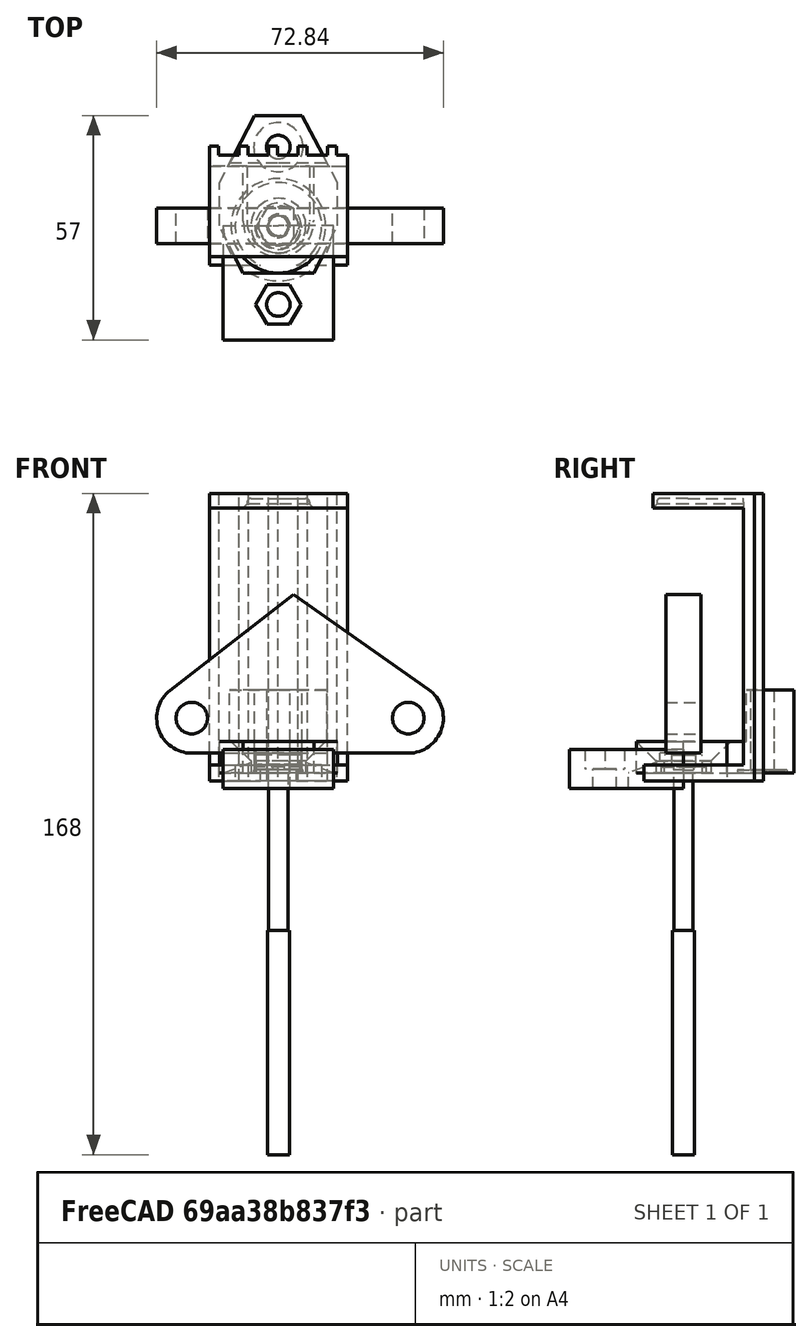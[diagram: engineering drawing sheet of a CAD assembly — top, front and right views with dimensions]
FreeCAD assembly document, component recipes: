
FREECAD ASSEMBLY — COMPONENT RECIPES ("stopper")

This assembly document has 6 components, labeled P0..P5 below (a component is one placed body or linked part). 5 of them carry a construction recipe — the FreeCAD feature program that regenerates the part from scratch, quoted from this document or its linked companion documents; the rest are supplied as boundary geometry only. No exploded tour is included for this assembly.
COMPONENT P0 — recipe-attached ("Body", modeled in this document).
Construction recipe (the document's own serialized feature program — sketch geometry with constraints, then the solid features built on it; lengths are millimeters unless a unit is written):

FEATURE [PartDesign::FeatureBase] BaseFeature
  BaseFeature = -> Extrude
  Suppressed = false
FEATURE [PartDesign::Body] Body004  label="Body"
  AllowCompound = false
  BaseFeature = -> Extrude
  Group = -> [BaseFeature]
  Origin = -> Origin005
  Tip = -> BaseFeature
COMPONENT P1 — geometry summary ("boss001"; no construction recipe available for this part):
  bounding box: 72.8 x 40.3 x 9.0 mm
  tessellated surface: 1,432 triangles
  volume: 16355 mm^3 (62% of its bounding box)
  symmetry: mirror-symmetric across its y mid-plane
COMPONENT P2 — recipe-attached ("fing001", modeled in this document).
Construction recipe (the document's own serialized feature program — sketch geometry with constraints, then the solid features built on it; lengths are millimeters unless a unit is written):

FEATURE [Sketcher::SketchObject] Sketch017  label="cope"
  ArcFitTolerance = 1e-06
  FullyConstrained = true
  MakeInternals = false
  Placement = pos=(0,0,0) rot=(1,0,0;1.5708rad)
  sketch-geometry (6):
    g0: LineSegment StartX=14 StartY=0 StartZ=0 EndX=6 EndY=3 EndZ=0
    g1: LineSegment StartX=6 StartY=3 StartZ=0 EndX=6 EndY=5 EndZ=0
    g2: LineSegment StartX=6 StartY=5 StartZ=0 EndX=0 EndY=5 EndZ=0
    g3: LineSegment StartX=14 StartY=0 StartZ=0 EndX=14 EndY=6 EndZ=0
    g4: LineSegment StartX=14 StartY=6 StartZ=0 EndX=0 EndY=6 EndZ=0
    g5: LineSegment StartX=0 StartY=6 StartZ=0 EndX=0 EndY=5 EndZ=0
  constraints (18):
    c: DistanceY(g0,g0) = 3
    c: Distance(g0,g-2) = 6
    c: Coincident(g0,g1)
    c: Vertical(g1)
    c: Coincident(g1,g2)
    c: PointOnObject(g2,g-2)
    c: Horizontal(g2)
    c: DistanceY(g1,g1) = 2
    c: PointOnObject(g0,g-1)
    c: DistanceX(g-1,g0) = 14
    c: Coincident(g0,g3)
    c: Vertical(g3)
    c: Coincident(g3,g4)
    c: PointOnObject(g4,g-2)
    c: Horizontal(g4)
    c: Coincident(g4,g5)
    c: Coincident(g5,g2)
    c: DistanceY(g3,g3) = 6
FEATURE [PartDesign::Revolution] Revolution
  Angle = 180
  Angle2 = 60
  Axis = (0,-2e-16,1)
  Base = (0,0,0)
  Placement = pos=(0,0,0) rot=(1,0,0;1.5708rad)
  Profile = -> Sketch017
  ReferenceAxis = -> Sketch017 [V_Axis]
  Reversed = true
  Suppressed = false
  Type = 0
FEATURE [Sketcher::SketchObject] Sketch018
  ArcFitTolerance = 1e-06
  AttachmentSupport = -> [Revolution]
  ExternalGeometry = -> [Revolution]
  FullyConstrained = true
  MakeInternals = false
  MapMode = 5
  Placement = pos=(0,0,6) rot=(0,0,1;3.14159rad)
  sketch-geometry (7):
    g0: LineSegment StartX=14 StartY=0 StartZ=0 EndX=14 EndY=29 EndZ=0
    g1: LineSegment StartX=14 StartY=29 StartZ=0 EndX=-14 EndY=29 EndZ=0
    g2: LineSegment StartX=-14 StartY=29 StartZ=0 EndX=-14 EndY=-3.6e-15 EndZ=0
    g3: GeomPoint X=0 Y=20 Z=0
    g4: GeomPoint X=0 Y=29 Z=0
    g5: GeomPoint X=0 Y=14 Z=0
    g6: ArcOfCircle CenterX=4.208e-13 CenterY=2.6e-15 CenterZ=0 NormalX=0 NormalY=0 NormalZ=1 AngleXU=0 Radius=14 StartAngle=0 EndAngle=3.14159
  constraints (15):
    c: Coincident(g0,g1)
    c: Coincident(g1,g2)
    c: Vertical(g0)
    c: Vertical(g2)
    c: Horizontal(g1)
    c: Coincident(g0,g-3)
    c: Coincident(g-4,g2)
    c: PointOnObject(g3,g-2)
    c: Symmetric(g1,g1,g4)
    c: DistanceY(g3,g4) = 9
    c: DistanceY(g-1,g3) = 20
    c: PointOnObject(g5,g-5)
    c: PointOnObject(g5,g-2)
    c: Perpendicular(g-3,g6) = 4.71239
    c: Coincident(g6,g2)
FEATURE [PartDesign::Pad] Pad011
  BaseFeature = -> Revolution
  Direction = (0,0,1)
  Length = 10
  Length2 = 10
  Placement = pos=(0,0,0) rot=(1,0,0;1.5708rad)
  Profile = -> Sketch018
  ReferenceAxis = -> Sketch018 [N_Axis]
  Reversed = true
  Suppressed = false
  Type = 0
FEATURE [Sketcher::SketchObject] Sketch019
  ArcFitTolerance = 1e-06
  AttachmentSupport = -> [Pad011]
  ExternalGeometry = -> [Pad011]
  FullyConstrained = true
  MakeInternals = false
  MapMode = 5
  Placement = pos=(0,0,6) rot=(0,0,1;3.14159rad)
  sketch-geometry (8):
    g0: GeomPoint X=0 Y=20 Z=0
    g1: LineSegment StartX=5.7735 StartY=20 StartZ=0 EndX=2.88675 EndY=25 EndZ=0
    g2: LineSegment StartX=2.88675 StartY=25 StartZ=0 EndX=-2.88675 EndY=25 EndZ=0
    g3: LineSegment StartX=-2.88675 StartY=25 StartZ=0 EndX=-5.7735 EndY=20 EndZ=0
    g4: LineSegment StartX=-5.7735 StartY=20 StartZ=0 EndX=-2.88675 EndY=15 EndZ=0
    g5: LineSegment StartX=-2.88675 StartY=15 StartZ=0 EndX=2.88675 EndY=15 EndZ=0
    g6: LineSegment StartX=2.88675 StartY=15 StartZ=0 EndX=5.7735 EndY=20 EndZ=0
    g7: Circle [constr] CenterX=0 CenterY=20 CenterZ=0 NormalX=0 NormalY=0 NormalZ=1 AngleXU=0 Radius=5.7735
  constraints (18):
    c: PointOnObject(g0,g-2)
    c: DistanceY(g-1,g0) = 20
    c: Coincident(g1,g2)
    c: Coincident(g2,g3)
    c: Coincident(g3,g4)
    c: Coincident(g4,g5)
    c: Coincident(g5,g6)
    c: Coincident(g6,g1)
    c: Equal(g1, g2-g6) x5
    c: PointOnObject(g1,g7)
    c: PointOnObject(g2,g7)
    c: PointOnObject(g3,g7)
    c: PointOnObject(g4,g7)
    c: PointOnObject(g5,g7)
    c: PointOnObject(g6,g7)
    c: Coincident(g7,g0)
    c: Horizontal(g2)
    c: Distance(g2,g1) = 10
FEATURE [PartDesign::Pocket] Pocket002
  BaseFeature = -> Pad011
  Direction = (0,0,-1)
  Length = 5
  Length2 = 5
  Placement = pos=(0,0,0) rot=(1,0,0;1.5708rad)
  Profile = -> Sketch019
  ReferenceAxis = -> Sketch019 [N_Axis]
  Suppressed = false
  Type = 0
FEATURE [Sketcher::SketchObject] Sketch020
  ArcFitTolerance = 1e-06
  AttachmentSupport = -> [Pocket002]
  FullyConstrained = true
  MakeInternals = false
  MapMode = 5
  Placement = pos=(0,0,1) rot=(0,0,1;3.14159rad)
  sketch-geometry (2):
    g0: GeomPoint X=0 Y=20 Z=0
    g1: Circle CenterX=0 CenterY=20 CenterZ=0 NormalX=0 NormalY=0 NormalZ=1 AngleXU=0 Radius=3
  constraints (4):
    c: PointOnObject(g0,g-2)
    c: DistanceY(g-1,g0) = 20
    c: Coincident(g1,g0)
    c: Diameter(g1) = 6
FEATURE [PartDesign::Pocket] Pocket003
  BaseFeature = -> Pocket002
  Direction = (0,0,-1)
  Length = 5
  Length2 = 5
  Placement = pos=(0,0,0) rot=(1,0,0;1.5708rad)
  Profile = -> Sketch020
  ReferenceAxis = -> Sketch020 [N_Axis]
  Suppressed = false
  Type = 0
FEATURE [PartDesign::Body] Body005  label="fing"
  AllowCompound = false
  Group = -> [Sketch017,Revolution,Sketch018,Pad011,Sketch019,Pocket002,Sketch020,Pocket003]
  Origin = -> Origin008
  Tip = -> Pocket003
COMPONENT P3 — recipe-attached ("bolt", modeled in this document).
Construction recipe (the document's own serialized feature program — sketch geometry with constraints, then the solid features built on it; lengths are millimeters unless a unit is written):

FEATURE [Sketcher::SketchObject] Sketch009  label="hd"
  ArcFitTolerance = 1e-06
  AttachmentSupport = -> [XY_Plane001]
  FullyConstrained = true
  MakeInternals = false
  MapMode = 5
  sketch-geometry (1):
    g0: Circle CenterX=0 CenterY=0 CenterZ=0 NormalX=0 NormalY=0 NormalZ=1 AngleXU=0 Radius=5.75
  constraints (2):
    c: Coincident(g0,g-1)
    c: Diameter(g0) = 11.5
FEATURE [PartDesign::Pad] Pad005
  Direction = (0,0,1)
  Length = 2.2
  Length2 = 10
  Profile = -> Sketch009 [Edge1]
  ReferenceAxis = -> Sketch009 [N_Axis]
  Suppressed = false
  Type = 0
FEATURE [Sketcher::SketchObject] Sketch010
  ArcFitTolerance = 1e-06
  AttachmentSupport = -> [Pad005]
  FullyConstrained = true
  MakeInternals = false
  MapMode = 5
  Placement = pos=(0,0,2.2) rot=(0,0,1;0rad)
  sketch-geometry (7):
    g0: LineSegment StartX=2.88675 StartY=0 StartZ=0 EndX=1.44338 EndY=2.5 EndZ=0
    g1: LineSegment StartX=1.44338 StartY=2.5 StartZ=0 EndX=-1.44338 EndY=2.5 EndZ=0
    g2: LineSegment StartX=-1.44338 StartY=2.5 StartZ=0 EndX=-2.88675 EndY=7.034e-13 EndZ=0
    g3: LineSegment StartX=-2.88675 StartY=7.034e-13 StartZ=0 EndX=-1.44338 EndY=-2.5 EndZ=0
    g4: LineSegment StartX=-1.44338 StartY=-2.5 StartZ=0 EndX=1.44338 EndY=-2.5 EndZ=0
    g5: LineSegment StartX=1.44338 StartY=-2.5 StartZ=0 EndX=2.88675 EndY=0 EndZ=0
    g6: Circle [constr] CenterX=0 CenterY=0 CenterZ=0 NormalX=0 NormalY=0 NormalZ=1 AngleXU=0 Radius=2.88675
  constraints (16):
    c: Coincident(g0,g1)
    c: Coincident(g1,g2)
    c: Coincident(g2,g3)
    c: Coincident(g3,g4)
    c: Coincident(g4,g5)
    c: Coincident(g5,g0)
    c: Equal(g0, g1-g5) x5
    c: PointOnObject(g0,g6)
    c: PointOnObject(g1,g6)
    c: PointOnObject(g2,g6)
    c: PointOnObject(g3,g6)
    c: PointOnObject(g4,g6)
    c: PointOnObject(g5,g6)
    c: Coincident(g6,g-1)
    c: PointOnObject(g5,g-1)
    c: DistanceY(g4,g0) = 5
FEATURE [PartDesign::Pocket] Pocket
  BaseFeature = -> Pad005
  Direction = (0,0,-1)
  Length = 1.4
  Length2 = 5
  Profile = -> Sketch010
  ReferenceAxis = -> Sketch010 [N_Axis]
  Suppressed = false
  Type = 0
FEATURE [PartDesign::Chamfer] Chamfer001
  Angle = 45
  Base = -> Pocket [Edge3]
  BaseFeature = -> Pocket
  ChamferType = 0
  FlipDirection = false
  Size = 0.7
  Size2 = 1
  SupportTransform = false
  Suppressed = false
  UseAllEdges = false
FEATURE [Sketcher::SketchObject] Sketch011
  ArcFitTolerance = 1e-06
  AttachmentSupport = -> [Chamfer001]
  FullyConstrained = true
  MakeInternals = false
  MapMode = 5
  Placement = pos=(0,0,0) rot=(1,0,0;3.14159rad)
  sketch-geometry (1):
    g0: Circle CenterX=0 CenterY=0 CenterZ=0 NormalX=0 NormalY=0 NormalZ=1 AngleXU=0 Radius=2.45
  constraints (2):
    c: Coincident(g0,g-1)
    c: Diameter(g0) = 4.9
FEATURE [PartDesign::Pad] Pad006
  BaseFeature = -> Chamfer001
  Direction = (0,0,-1)
  Length = 40
  Length2 = 10
  Profile = -> Sketch011
  ReferenceAxis = -> Sketch011 [N_Axis]
  Suppressed = false
  Type = 0
FEATURE [Sketcher::SketchObject] Sketch012
  ArcFitTolerance = 1e-06
  AttachmentSupport = -> [Pad006]
  FullyConstrained = true
  MakeInternals = false
  MapMode = 5
  Placement = pos=(0,0,-40) rot=(1,0,0;3.14159rad)
  sketch-geometry (1):
    g0: Circle CenterX=0 CenterY=0 CenterZ=0 NormalX=0 NormalY=0 NormalZ=1 AngleXU=0 Radius=2.8
  constraints (2):
    c: Coincident(g0,g-1)
    c: Diameter(g0) = 5.6
FEATURE [PartDesign::Pad] Pad007
  BaseFeature = -> Pad006
  Direction = (0,0,-1)
  Length = 57
  Length2 = 10
  Profile = -> Sketch012
  ReferenceAxis = -> Sketch012 [N_Axis]
  Suppressed = false
  Type = 0
FEATURE [PartDesign::Body] Body001  label="m6"
  AllowCompound = false
  Group = -> [Sketch009,Pad005,Sketch010,Pocket,Chamfer001,Sketch011,Pad006,Sketch012,Pad007]
  Origin = -> Origin001
  Tip = -> Pad007
COMPONENT P4 — recipe-attached ("nut", modeled in this document).
Construction recipe (the document's own serialized feature program — sketch geometry with constraints, then the solid features built on it; lengths are millimeters unless a unit is written):

FEATURE [Sketcher::SketchObject] Sketch013
  ArcFitTolerance = 1e-06
  AttachmentSupport = -> [XY_Plane002]
  FullyConstrained = true
  MakeInternals = false
  MapMode = 5
  sketch-geometry (8):
    g0: LineSegment StartX=5.54256 StartY=0 StartZ=0 EndX=2.77128 EndY=4.8 EndZ=0
    g1: LineSegment StartX=2.77128 StartY=4.8 StartZ=0 EndX=-2.77128 EndY=4.8 EndZ=0
    g2: LineSegment StartX=-2.77128 StartY=4.8 StartZ=0 EndX=-5.54256 EndY=-9e-16 EndZ=0
    g3: LineSegment StartX=-5.54256 StartY=-9e-16 StartZ=0 EndX=-2.77128 EndY=-4.8 EndZ=0
    g4: LineSegment StartX=-2.77128 StartY=-4.8 StartZ=0 EndX=2.77128 EndY=-4.8 EndZ=0
    g5: LineSegment StartX=2.77128 StartY=-4.8 StartZ=0 EndX=5.54256 EndY=0 EndZ=0
    g6: Circle [constr] CenterX=0 CenterY=0 CenterZ=0 NormalX=0 NormalY=0 NormalZ=1 AngleXU=0 Radius=5.54256
    g7: Circle CenterX=0 CenterY=0 CenterZ=0 NormalX=0 NormalY=0 NormalZ=1 AngleXU=0 Radius=3
  constraints (18):
    c: Coincident(g0,g1)
    c: Coincident(g1,g2)
    c: Coincident(g2,g3)
    c: Coincident(g3,g4)
    c: Coincident(g4,g5)
    c: Coincident(g5,g0)
    c: Equal(g0, g1-g5) x5
    c: PointOnObject(g0,g6)
    c: PointOnObject(g1,g6)
    c: PointOnObject(g2,g6)
    c: PointOnObject(g3,g6)
    c: PointOnObject(g4,g6)
    c: PointOnObject(g5,g6)
    c: Coincident(g6,g-1)
    c: PointOnObject(g5,g-1)
    c: DistanceY(g4,g0) = 9.6  'tenish'
    c: Coincident(g7,g6)
    c: Diameter(g7) = 6
FEATURE [PartDesign::Pad] Pad008
  Direction = (0,0,1)
  Length = 4.6
  Length2 = 10
  Profile = -> Sketch013
  ReferenceAxis = -> Sketch013 [N_Axis]
  Suppressed = false
  Type = 0
FEATURE [PartDesign::Body] Body002  label="m6b"
  AllowCompound = false
  Group = -> [Sketch013,Pad008]
  Origin = -> Origin002
  Tip = -> Pad008
COMPONENT P5 — recipe-attached ("tailhk001", modeled in this document).
Construction recipe (the document's own serialized feature program — sketch geometry with constraints, then the solid features built on it; lengths are millimeters unless a unit is written):

FEATURE [Sketcher::SketchObject] Sketch014
  ArcFitTolerance = 1e-06
  AttachmentSupport = -> [XY_Plane004]
  FullyConstrained = true
  MakeInternals = false
  MapMode = 5
  sketch-geometry (12):
    g0: Circle CenterX=0 CenterY=0 CenterZ=0 NormalX=0 NormalY=0 NormalZ=1 AngleXU=0 Radius=7
    g1: Circle CenterX=0 CenterY=20 CenterZ=0 NormalX=0 NormalY=0 NormalZ=1 AngleXU=0 Radius=3
    g2: LineSegment StartX=0 StartY=-12 StartZ=0 EndX=9 EndY=-12 EndZ=0
    g3: LineSegment StartX=9 StartY=-12 StartZ=0 EndX=15 EndY=0 EndZ=0
    g4: LineSegment StartX=15 StartY=0 StartZ=0 EndX=15 EndY=11 EndZ=0
    g5: LineSegment StartX=15 StartY=11 StartZ=0 EndX=6 EndY=28 EndZ=0
    g6: LineSegment StartX=6 StartY=28 StartZ=0 EndX=0 EndY=28 EndZ=0
    g7: LineSegment StartX=-6 StartY=28 StartZ=0 EndX=0 EndY=28 EndZ=0
    g8: LineSegment StartX=-15 StartY=11 StartZ=0 EndX=-6 EndY=28 EndZ=0
    g9: LineSegment StartX=-15 StartY=0 StartZ=0 EndX=-15 EndY=11 EndZ=0
    g10: LineSegment StartX=-9 StartY=-12 StartZ=0 EndX=-15 EndY=0 EndZ=0
    g11: LineSegment StartX=-9 StartY=-12 StartZ=0 EndX=0 EndY=-12 EndZ=0
  constraints (31):
    c: Coincident(g0,g-1)
    c: Diameter(g0) = 14
    c: PointOnObject(g1,g-2)
    c: DistanceY(g0,g1) = 20
    c: Diameter(g1) = 6
    c: PointOnObject(g2,g-2)
    c: Horizontal(g2)
    c: Coincident(g2,g3)
    c: Coincident(g3,g4)
    c: Coincident(g4,g5)
    c: Coincident(g5,g6)
    c: PointOnObject(g6,g-2)
    c: Horizontal(g6)
    c: DistanceX(g6,g6) = 6
    c: DistanceY(g1,g6) = 8
    c: DistanceX(g-1,g4) = 15
    c: Vertical(g4)
    c: DistanceY(g2,g0) = 12
    c: PointOnObject(g3,g-1)
    c: DistanceX(g2,g2) = 9
    c: DistanceY(g3,g4) = 11
    c: Symmetric(g3,g10,g-2)
    c: Symmetric(g3,g10,g-2)
    c: Symmetric(g4,g9,g-2)
    c: Symmetric(g4,g9,g-2)
    c: Symmetric(g5,g8,g-2)
    c: Symmetric(g5,g8,g-2)
    c: Symmetric(g6,g7,g-2)
    c: Coincident(g11,g10)
    c: Coincident(g11,g2)
    c: Coincident(g7,g6)
FEATURE [PartDesign::Pad] Pad009
  Direction = (0,0,1)
  Length = 8
  Length2 = 10
  Profile = -> Sketch014
  ReferenceAxis = -> Sketch014 [N_Axis]
  Suppressed = false
  Type = 0
FEATURE [Sketcher::SketchObject] Sketch015
  ArcFitTolerance = 1e-06
  AttachmentSupport = -> [Pad009]
  ExternalGeometry = -> [Pad009]
  FullyConstrained = true
  MakeInternals = false
  MapMode = 5
  Placement = pos=(0,0,0) rot=(1,0,0;3.14159rad)
  sketch-geometry (1):
    g0: Circle CenterX=0 CenterY=-20 CenterZ=0 NormalX=0 NormalY=0 NormalZ=1 AngleXU=0 Radius=6.25
  constraints (2):
    c: Coincident(g0,g-3)
    c: Diameter(g0) = 12.5
FEATURE [PartDesign::Pocket] Pocket001
  BaseFeature = -> Pad009
  Direction = (0,0,1)
  Length = 0.8
  Length2 = 5
  Profile = -> Sketch015
  ReferenceAxis = -> Sketch015 [N_Axis]
  Suppressed = false
  Type = 0
FEATURE [PartDesign::Chamfer] Chamfer002
  Angle = 45
  Base = -> Pocket001 [Edge27]
  BaseFeature = -> Pocket001
  ChamferType = 2
  FlipDirection = false
  Size = 5
  Size2 = 1
  SupportTransform = false
  Suppressed = false
  UseAllEdges = false
FEATURE [Sketcher::SketchObject] Sketch016
  ArcFitTolerance = 1e-06
  AttachmentSupport = -> [Chamfer002]
  ExternalGeometry = -> [Chamfer002]
  FullyConstrained = true
  MakeInternals = false
  MapMode = 5
  Placement = pos=(0,0,8) rot=(0,0,1;0rad)
  sketch-geometry (6):
    g0: Circle CenterX=0 CenterY=20 CenterZ=0 NormalX=0 NormalY=0 NormalZ=1 AngleXU=0 Radius=3
    g1: LineSegment StartX=0 StartY=16 StartZ=0 EndX=12.3529 EndY=16 EndZ=0
    g2: LineSegment StartX=12.3529 StartY=16 StartZ=0 EndX=6 EndY=28 EndZ=0
    g3: LineSegment StartX=6 StartY=28 StartZ=0 EndX=-6 EndY=28 EndZ=0
    g4: LineSegment StartX=-6 StartY=28 StartZ=0 EndX=-12.3529 EndY=16 EndZ=0
    g5: LineSegment StartX=-12.3529 StartY=16 StartZ=0 EndX=0 EndY=16 EndZ=0
  constraints (15):
    c: Equal(g-3,g0)
    c: PointOnObject(g1,g-2)
    c: PointOnObject(g1,g-6)
    c: Horizontal(g1)
    c: Coincident(g1,g2)
    c: Coincident(g2,g-6)
    c: Coincident(g2,g3)
    c: Coincident(g3,g-7)
    c: Coincident(g3,g4)
    c: PointOnObject(g4,g-7)
    c: Coincident(g4,g5)
    c: Coincident(g5,g1)
    c: Horizontal(g5)
    c: DistanceY(g1,g0) = 4
    c: Coincident(g0,g-3)
FEATURE [PartDesign::Pad] Pad010
  BaseFeature = -> Chamfer002
  Direction = (0,0,1)
  Length = 13
  Length2 = 10
  Profile = -> Sketch016
  ReferenceAxis = -> Sketch016 [N_Axis]
  Suppressed = false
  Type = 0
FEATURE [PartDesign::Body] Body003  label="tailhk"
  AllowCompound = false
  Group = -> [Sketch014,Pad009,Sketch015,Pocket001,Chamfer002,Sketch016,Pad010]
  Origin = -> Origin004
  Tip = -> Pad010
PROVENANCE & LICENSES
A FreeCAD (.FCStd) document from a public repository crawl; recipes are the document's own serialized feature recipes (and, for linked parts, companion documents' recipes).
License: bsd.
